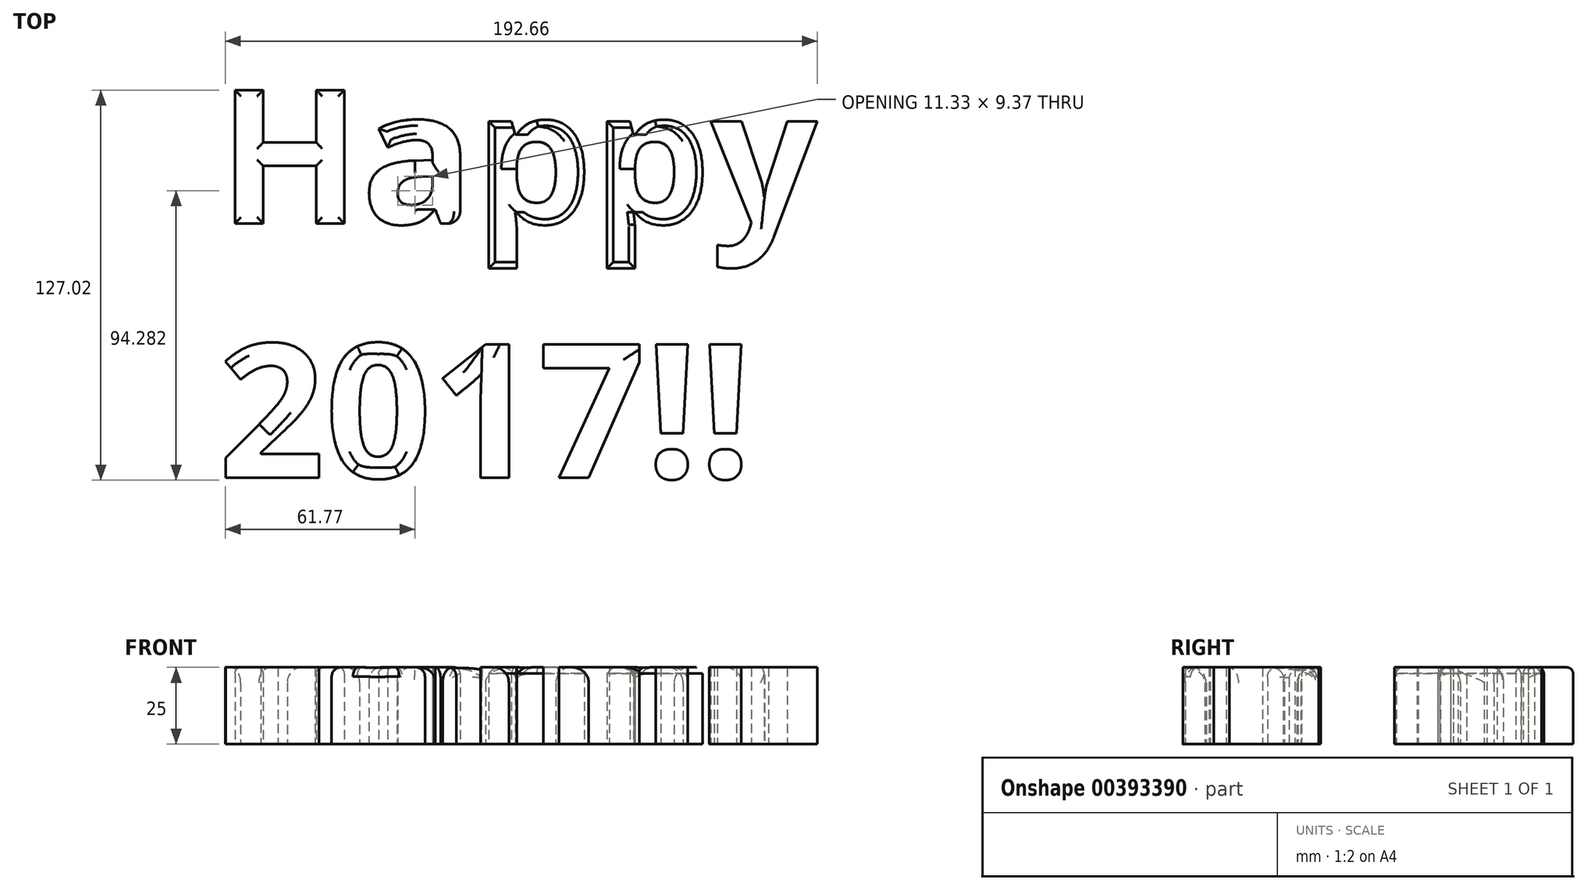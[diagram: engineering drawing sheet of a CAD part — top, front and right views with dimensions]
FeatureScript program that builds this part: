
annotation { "Feature Type Name" : "Feature", "Feature Type Description" : "" }
export const myFeature = defineFeature(function(context is Context, id is Id, definition is map)
    precondition{}
    {
        {
            var Q0;
            Q0=qCreatedBy(makeId("Top.planeOp"),FACE);
            var sketch = newSketch(context, id + "F0", { "sketchPlane" : qUnion([Q0])});
            skText(sketch, "E0", { "text": "Happy\n2017!!", "fontName": "OpenSans-Bold.ttf"});
            const initialGuessF0  = {"E0": [-0.07033, 0.0259, 1, 0, 0.04382]};
            skSetInitialGuess(sketch, initialGuessF0);
            skSolve(sketch);
        }
        {
            var Q0;
            Q0 = qSketchRegion(id + "F0", true);
            extrude(context, id + "F1", {"entities" : qUnion([Q0]), "depth" : 25 * mm});
        }
        {
            var Q0;
            Q0=makeQuery(id+"F1.opExtrude","CAP_EDGE",EDGE,{"disambiguationData":[OSD([sQuery(id+"F0.wireOp",EDGE,"E0.sketch_text.stroke-5")])],"isStart":false});
            var Q1;
            Q1=makeQuery(id+"F1.opExtrude","CAP_EDGE",EDGE,{"disambiguationData":[OSD([sQuery(id+"F0.wireOp",EDGE,"E0.sketch_text.stroke-6")])],"isStart":false});
            var Q2;
            Q2=makeQuery(id+"F1.opExtrude","CAP_EDGE",EDGE,{"disambiguationData":[OSD([sQuery(id+"F0.wireOp",EDGE,"E0.sketch_text.stroke-7")])],"isStart":false});
            var Q3;
            Q3=makeQuery(id+"F1.opExtrude","CAP_EDGE",EDGE,{"disambiguationData":[OSD([sQuery(id+"F0.wireOp",EDGE,"E0.sketch_text.stroke-8")])],"isStart":false});
            var Q4;
            Q4=makeQuery(id+"F1.opExtrude","CAP_EDGE",EDGE,{"disambiguationData":[OSD([sQuery(id+"F0.wireOp",EDGE,"E0.sketch_text.stroke-3")])],"isStart":false});
            var Q5;
            Q5=makeQuery(id+"F1.opExtrude","CAP_EDGE",EDGE,{"disambiguationData":[OSD([sQuery(id+"F0.wireOp",EDGE,"E0.sketch_text.stroke-4")])],"isStart":false});
            var Q6;
            Q6=makeQuery(id+"F1.opExtrude","CAP_EDGE",EDGE,{"disambiguationData":[OSD([sQuery(id+"F0.wireOp",EDGE,"E0.sketch_text.stroke-2")])],"isStart":false});
            var Q7;
            Q7=makeQuery(id+"F1.opExtrude","CAP_EDGE",EDGE,{"disambiguationData":[OSD([sQuery(id+"F0.wireOp",EDGE,"E0.sketch_text.stroke-1")])],"isStart":false});
            var Q8;
            Q8=makeQuery(id+"F1.opExtrude","CAP_EDGE",EDGE,{"disambiguationData":[OSD([sQuery(id+"F0.wireOp",EDGE,"E0.sketch_text.stroke-9")])],"isStart":false});
            var Q9;
            Q9=makeQuery(id+"F1.opExtrude","CAP_EDGE",EDGE,{"disambiguationData":[OSD([sQuery(id+"F0.wireOp",EDGE,"E0.sketch_text.stroke-10")])],"isStart":false});
            var Q10;
            Q10=makeQuery(id+"F1.opExtrude","CAP_EDGE",EDGE,{"disambiguationData":[OSD([sQuery(id+"F0.wireOp",EDGE,"E0.sketch_text.stroke-11")])],"isStart":false});
            var Q11;
            Q11=makeQuery(id+"F1.opExtrude","CAP_EDGE",EDGE,{"disambiguationData":[OSD([sQuery(id+"F0.wireOp",EDGE,"E0.sketch_text.stroke-0")])],"isStart":false});
            var Q12;
            Q12=makeQuery(id+"F1.opExtrude","CAP_EDGE",EDGE,{"disambiguationData":[OSD([sQuery(id+"F0.wireOp",EDGE,"E0.sketch_text.stroke-25")])],"isStart":false});
            var Q13;
            Q13=makeQuery(id+"F1.opExtrude","CAP_EDGE",EDGE,{"disambiguationData":[OSD([sQuery(id+"F0.wireOp",EDGE,"E0.sketch_text.stroke-23")])],"isStart":false});
            var Q14;
            Q14=makeQuery(id+"F1.opExtrude","CAP_EDGE",EDGE,{"disambiguationData":[OSD([sQuery(id+"F0.wireOp",EDGE,"E0.sketch_text.stroke-24")])],"isStart":false});
            fillet(context, id + "F2", {"entities" : qUnion([Q0, Q1, Q2, Q3, Q4, Q5, Q6, Q7, Q8, Q9, Q10, Q11, Q12, Q13, Q14]), "radius" : 2 * mm, "tangentPropagation" : true, "allowEdgeOverflow" : false});
        }
        {
            var Q0;
            Q0=makeQuery(id+"F1.opExtrude","CAP_EDGE",EDGE,{"disambiguationData":[OSD([sQuery(id+"F0.wireOp",EDGE,"E0.sketch_text.stroke-19")])],"isStart":false});
            var Q1;
            Q1=makeQuery(id+"F1.opExtrude","CAP_EDGE",EDGE,{"disambiguationData":[OSD([sQuery(id+"F0.wireOp",EDGE,"E0.sketch_text.stroke-29")])],"isStart":false});
            fillet(context, id + "F3", {"entities" : qUnion([Q0, Q1]), "radius" : 4 * mm, "tangentPropagation" : true, "allowEdgeOverflow" : false});
        }
        {
            var Q0;
            Q0=makeQuery(id+"F1.opExtrude","CAP_EDGE",EDGE,{"disambiguationData":[OSD([sQuery(id+"F0.wireOp",EDGE,"E0.sketch_text.stroke-55")])],"isStart":false});
            var Q1;
            Q1=makeQuery(id+"F1.opExtrude","CAP_EDGE",EDGE,{"disambiguationData":[OSD([sQuery(id+"F0.wireOp",EDGE,"E0.sketch_text.stroke-78")])],"isStart":false});
            var Q2;
            Q2=makeQuery(id+"F1.opExtrude","CAP_EDGE",EDGE,{"disambiguationData":[OSD([sQuery(id+"F0.wireOp",EDGE,"E0.sketch_text.stroke-139")])],"isStart":false});
            var Q3;
            Q3=makeQuery(id+"F1.opExtrude","CAP_EDGE",EDGE,{"disambiguationData":[OSD([sQuery(id+"F0.wireOp",EDGE,"E0.sketch_text.stroke-103")])],"isStart":false});
            var Q4;
            Q4=makeQuery(id+"F1.opExtrude","CAP_EDGE",EDGE,{"disambiguationData":[OSD([sQuery(id+"F0.wireOp",EDGE,"E0.sketch_text.stroke-153")])],"isStart":false});
            var Q5;
            Q5=makeQuery(id+"F1.opExtrude","CAP_EDGE",EDGE,{"disambiguationData":[OSD([sQuery(id+"F0.wireOp",EDGE,"E0.sketch_text.stroke-155")])],"isStart":false});
            var Q6;
            Q6=makeQuery(id+"F1.opExtrude","CAP_EDGE",EDGE,{"disambiguationData":[OSD([sQuery(id+"F0.wireOp",EDGE,"E0.sketch_text.stroke-149")])],"isStart":false});
            var Q7;
            Q7=makeQuery(id+"F1.opExtrude","CAP_EDGE",EDGE,{"disambiguationData":[OSD([sQuery(id+"F0.wireOp",EDGE,"E0.sketch_text.stroke-147")])],"isStart":false});
            var Q8;
            Q8=makeQuery(id+"F1.opExtrude","CAP_EDGE",EDGE,{"disambiguationData":[OSD([sQuery(id+"F0.wireOp",EDGE,"E0.sketch_text.stroke-84")])],"isStart":false});
            var Q9;
            Q9=makeQuery(id+"F1.opExtrude","CAP_EDGE",EDGE,{"disambiguationData":[OSD([sQuery(id+"F0.wireOp",EDGE,"E0.sketch_text.stroke-160")])],"isStart":false});
            fillet(context, id + "F4", {"entities" : qUnion([Q0, Q1, Q2, Q3, Q4, Q5, Q6, Q7, Q8, Q9]), "radius" : 5 * mm, "tangentPropagation" : true, "allowEdgeOverflow" : false});
        }
        {
            var Q0;
            Q0=makeQuery(id+"F1.opExtrude","CAP_EDGE",EDGE,{"disambiguationData":[OSD([sQuery(id+"F0.wireOp",EDGE,"E0.sketch_text.stroke-42")])],"isStart":false});
            var Q1;
            Q1=makeQuery(id+"F1.opExtrude","CAP_EDGE",EDGE,{"disambiguationData":[OSD([sQuery(id+"F0.wireOp",EDGE,"E0.sketch_text.stroke-50")])],"isStart":false});
            var Q2;
            Q2=makeQuery(id+"F1.opExtrude","CAP_EDGE",EDGE,{"disambiguationData":[OSD([sQuery(id+"F0.wireOp",EDGE,"E0.sketch_text.stroke-73")])],"isStart":false});
            var Q3;
            Q3=makeQuery(id+"F1.opExtrude","CAP_EDGE",EDGE,{"disambiguationData":[OSD([sQuery(id+"F0.wireOp",EDGE,"E0.sketch_text.stroke-65")])],"isStart":false});
            var Q4;
            Q4=makeQuery(id+"F1.opExtrude","CAP_EDGE",EDGE,{"disambiguationData":[OSD([sQuery(id+"F0.wireOp",EDGE,"E0.sketch_text.stroke-64")])],"isStart":false});
            var Q5;
            Q5=makeQuery(id+"F1.opExtrude","CAP_EDGE",EDGE,{"disambiguationData":[OSD([sQuery(id+"F0.wireOp",EDGE,"E0.sketch_text.stroke-63")])],"isStart":false});
            var Q6;
            Q6=makeQuery(id+"F1.opExtrude","CAP_EDGE",EDGE,{"disambiguationData":[OSD([sQuery(id+"F0.wireOp",EDGE,"E0.sketch_text.stroke-41")])],"isStart":false});
            var Q7;
            Q7=makeQuery(id+"F1.opExtrude","CAP_EDGE",EDGE,{"disambiguationData":[OSD([sQuery(id+"F0.wireOp",EDGE,"E0.sketch_text.stroke-43")])],"isStart":false});
            var Q8;
            Q8=makeQuery(id+"F1.opExtrude","CAP_EDGE",EDGE,{"disambiguationData":[OSD([sQuery(id+"F0.wireOp",EDGE,"E0.sketch_text.stroke-66")])],"isStart":false});
            chamfer(context, id + "F5", {"entities" : qUnion([Q0, Q1, Q2, Q3, Q4, Q5, Q6, Q7, Q8]), "width" : 2 * mm, "tangentPropagation" : true});
        }
        {
            var Q0;
            Q0=makeQuery(id+"F1.opExtrude","CAP_EDGE",EDGE,{"disambiguationData":[OSD([sQuery(id+"F0.wireOp",EDGE,"E0.sketch_text.stroke-131")])],"isStart":false});
            var Q1;
            Q1=makeQuery(id+"F1.opExtrude","CAP_EDGE",EDGE,{"disambiguationData":[OSD([sQuery(id+"F0.wireOp",EDGE,"E0.sketch_text.stroke-145")])],"isStart":false});
            fillet(context, id + "F6", {"entities" : qUnion([Q0, Q1]), "radius" : 3 * mm, "tangentPropagation" : true, "allowEdgeOverflow" : false});
        }
    });
